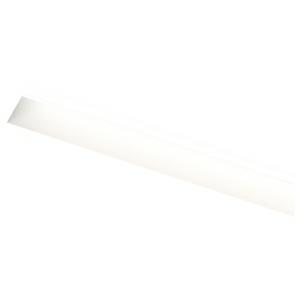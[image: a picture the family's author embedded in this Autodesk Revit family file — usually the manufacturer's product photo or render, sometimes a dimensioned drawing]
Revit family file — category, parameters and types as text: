
# Revit family: groove_l_1160_rl_led_21w_3000k_1364lm_cri80_130-0500_50bc
name_source: partatom
category: Leuchten
revit_build: Autodesk Revit 2016 (Build: 20190508_0715(x64)
units: mm (PartAtom-declared; Revit-internal decimal feet)

## family parameters
Basisbauteil = Fläche
Beim Laden mit Abzugskörper schneiden = Nein
Bemaßung runder Anschluss = Durchmesser verwenden
Gemeinsam genutzt = Nein
Lichtquelle = Nein
Raumberechnungspunkt = Nein
Teiletyp = Normal

## types (1)
- 130-0500- (4 x LED, 710 lm, 5.1 W, 3000K)
    Beschreibung = The rimless luminaire GROOVE from the familiy GROOVE consists of aluminum-extruded profile. Charming SOFT-EDGE design ensure unparalleled styling. The ballast is integrated and allows for an operation with 220-240V (50.60Hz). GROOVE (# 130-0500) ist not dimmable (on/off). The luminaire with direct illumination and corresponds to protection class SK1 at IP20.
    CIE Flux Codes = 59 87 97 100 49
    Color Rendering = 1B/80…89
    Color Temperature = 3000K
    Height = 0 mm  [stored 0 ft]
    Hersteller = Prolicht
    Lamp Light Flux = 710 lm
    Lamp Power = 5.1 W
    Lamp count = 4
    Lampe = 4 x LED
    Length = 1160 mm
    Luminous efficacy = 67 lm/W
    ModVariant = Nein
    Modell = 130-0500
    Mounting Place = Ceiling
    Mounting Type = Recessed
    Number of Poles = 1
    OnlyDefault = Ja
    Power Factor = 1
    Product Name = GROOVE L=1160 RL LED 21W 3000K 1364lm CRI80
    Product group = Trimless recessed profile lights
    ProductGroupID = 413
    Protection Class = Protection class
    Protection Degree = Degree of protection
    RLX_Detail_Level = 1
    RlxData = <blob elided: 133685 chars, md5=2e750a80>
    Scheinlast = 20 VA
    Socket = socket
    Standby Power = 0 W
    System Light Flux = 1370 lm
    System Power = 20 W
    Typenbild = 130-0500.jpg
    URL = http://relux.com
    VarID = 130-0500-
    Voltage = 0 V
    Vorgabe-Ansicht = 1800 mm
    Weight = 0.00 kg
    Width = 75 mm

note: [stored X ft] marks values corroborated as IEEE doubles in the binary element streams (Revit-internal decimal feet)

## geometry (parser evidence)
native form markers: Blend x4, Sweep x13
no freeform markers — native parametric forms only
